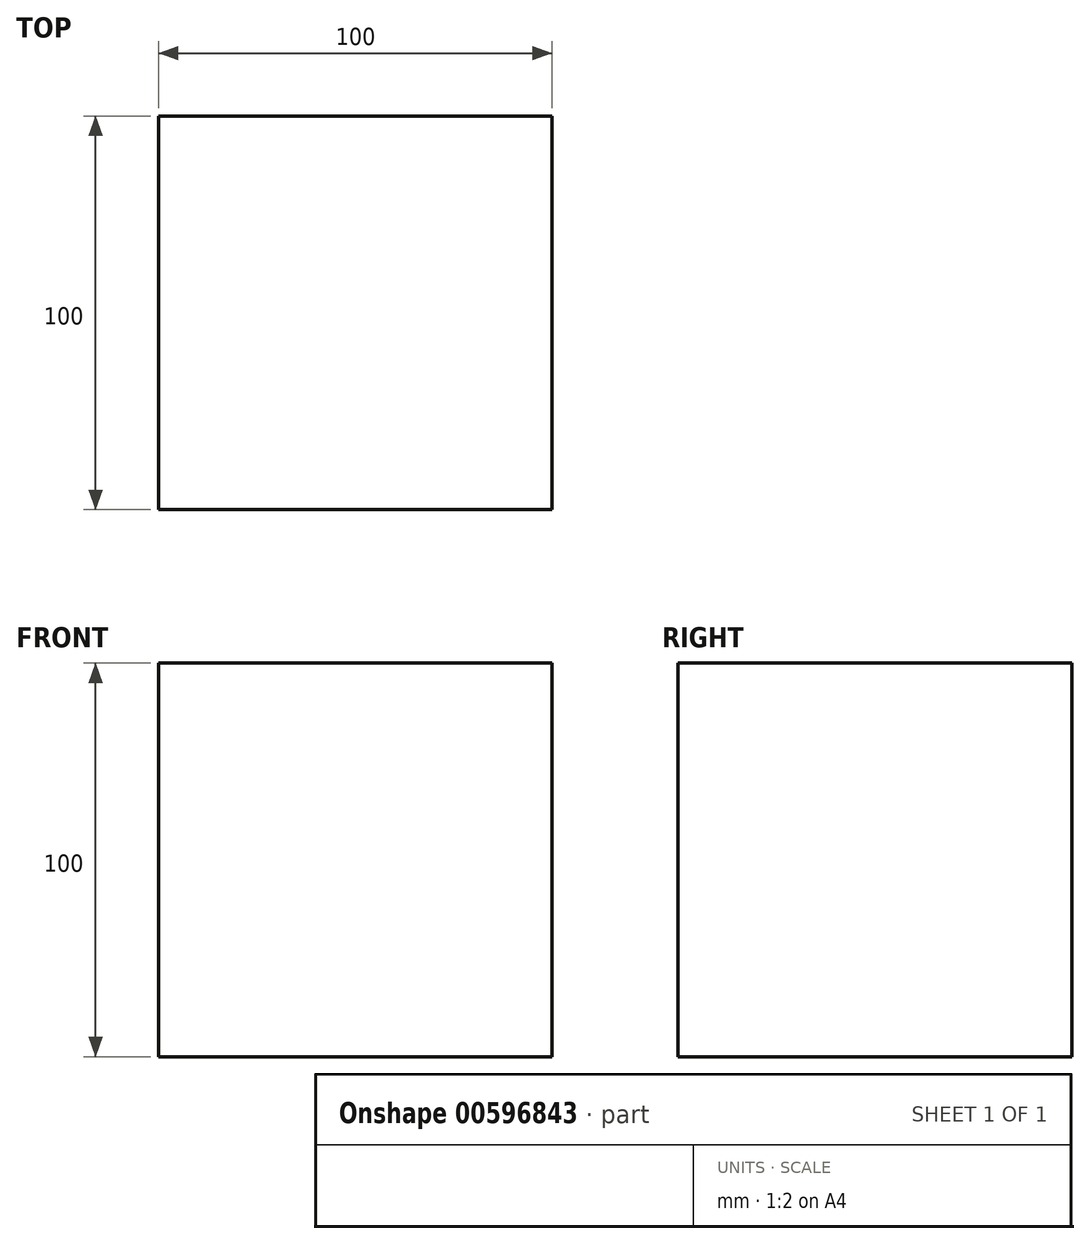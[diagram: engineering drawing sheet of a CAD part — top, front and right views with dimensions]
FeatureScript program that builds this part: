
annotation { "Feature Type Name" : "Feature", "Feature Type Description" : "" }
export const myFeature = defineFeature(function(context is Context, id is Id, definition is map)
    precondition{}
    {
        {
            var Q0;
            Q0=qCreatedBy(makeId("Top.planeOp"),FACE);
            var sketch = newSketch(context, id + "F0", { "sketchPlane" : qUnion([Q0])});
            skLineSegment(sketch, "E0.bottom", {"start": v(50, 50) * mm, "end": v(-50, 50) * mm});
            skLineSegment(sketch, "E0.top", {"start": v(50, -50) * mm, "end": v(-50, -50) * mm});
            skLineSegment(sketch, "E0.left", {"start": v(50, 50) * mm, "end": v(50, -50) * mm});
            skLineSegment(sketch, "E0.right", {"start": v(-50, 50) * mm, "end": v(-50, -50) * mm});
            skPoint(sketch, "E0.middle", {"position": v(0, 0) * mm});
            skSolve(sketch);
        }
        {
            var Q0;
            Q0=makeQuery(id+"F0.imprint","IMPRINT",FACE,{"disambiguationData":[TD([[makeQuery(id+"F0.imprint","IMPRINT",EDGE,{"derivedFrom":sQuery(id+"F0.wireOp",EDGE,"E0.bottom")}),1.0]])]});
            extrude(context, id + "F1", {"entities" : qUnion([Q0]), "endBound" : BoundingType.SYMMETRIC, "depth" : 100 * mm, "offsetDistance" : 25 * mm});
        }
    });
